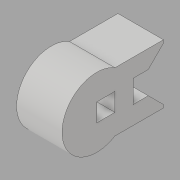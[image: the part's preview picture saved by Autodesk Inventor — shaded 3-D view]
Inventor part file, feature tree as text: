
AUTODESK INVENTOR PART (.ipt)
format: ipt  version: 2017 (Build 210142000, 142)  size: 104,960 bytes
history: native  units: in
note: dims shown in document units (in); Inventor stores cm internally (conversion verified against a paired STEP export)
features: extrude x2, sketch x2, chamfer x1
ambient origin geometry x8: Origin, YZ Plane, XZ Plane, XY Plane, X Axis, Y Axis, Z Axis, Center Point
bodies: Solid1 (feature_tree)
feature tree (5):
  extrude  "Extrusion1"  Depth=0.2in
  extrude  "Extrusion2"  Depth=0.15in
  chamfer  "Chamfer1"  Distance=0.3in
  sketch  "Sketch1"  dims[d0=0.12in d1=0.2in]
  sketch  "Sketch2"  dims[d3=0.12in d4=0.15in d5=0.3in d6=0.0in d7=0.12in d8=0.3in d9=0.0in d10=0.1in d11=0.125in d12=45.0deg]
